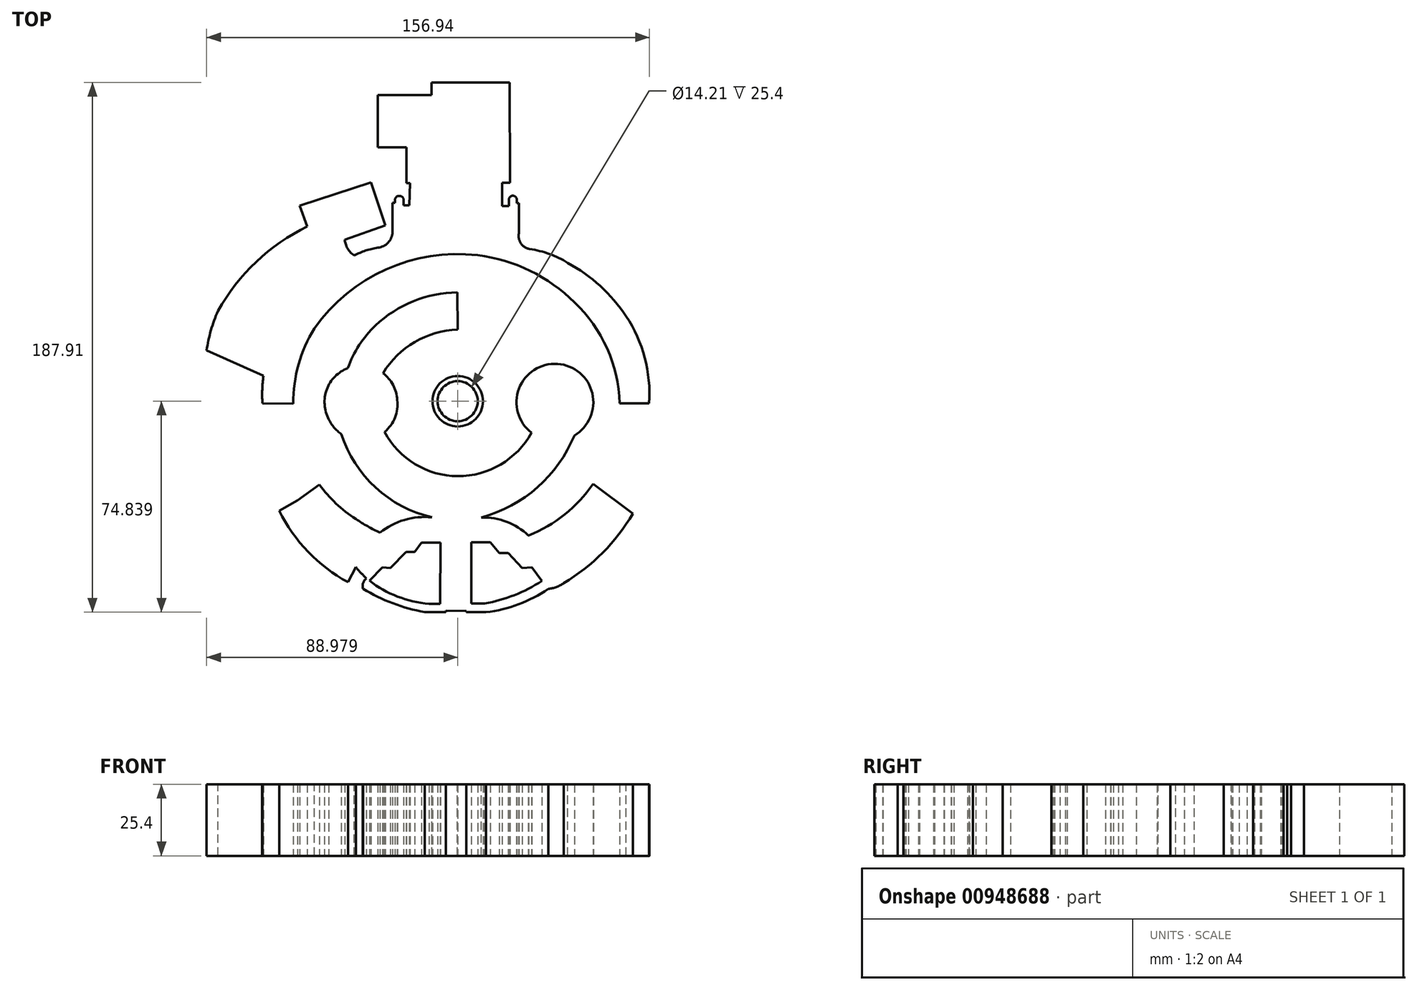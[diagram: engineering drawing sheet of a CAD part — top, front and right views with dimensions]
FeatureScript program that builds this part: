
annotation { "Feature Type Name" : "Feature", "Feature Type Description" : "" }
export const myFeature = defineFeature(function(context is Context, id is Id, definition is map)
    precondition{}
    {
        {
            var Q0;
            Q0=qCreatedBy(makeId("Top.planeOp"),FACE);
            var sketch = newSketch(context, id + "F0", { "sketchPlane" : qUnion([Q0])});
            skArc(sketch, "E0", {"start": v(181.34, -72.89) * mm, "mid": v(195.13, -62.13) * mm, "end": v(205.83, -48.3) * mm});
            skLineSegment(sketch, "E1", {"start": v(191.68, -37.7) * mm, "end": v(205.83, -48.3) * mm});
            skArc(sketch, "E2", {"start": v(163.15, -57.94) * mm, "mid": v(183.04, -47.44) * mm, "end": v(196.42, -29.36) * mm});
            skArc(sketch, "E3", {"start": v(185.16, 26.63) * mm, "mid": v(169.38, 37.88) * mm, "end": v(150.8, 43.4) * mm});
            skArc(sketch, "E4", {"start": v(150.8, 43.4) * mm, "mid": v(118.33, 38.35) * mm, "end": v(92.98, 17.42) * mm});
            skArc(sketch, "E5", {"start": v(92.98, 17.42) * mm, "mid": v(85.82, -2.9) * mm, "end": v(87.93, -24.34) * mm});
            skArc(sketch, "E6", {"start": v(87.91, -24.4) * mm, "mid": v(95.52, -39.01) * mm, "end": v(107.64, -50.16) * mm});
            skArc(sketch, "E7", {"start": v(107.64, -50.16) * mm, "mid": v(112.67, -53.24) * mm, "end": v(117.97, -55.82) * mm});
            skArc(sketch, "E8", {"start": v(181.34, -72.89) * mm, "mid": v(176.23, -63.57) * mm, "end": v(168.82, -55.95) * mm});
            skArc(sketch, "E9", {"start": v(168.82, -55.95) * mm, "mid": v(161.1, -51.17) * mm, "end": v(152.17, -49.6) * mm});
            skArc(sketch, "E10", {"start": v(134.6, -49.59) * mm, "mid": v(119, -53.1) * mm, "end": v(108.7, -65.31) * mm});
            skArc(sketch, "E11", {"start": v(86.91, -43.6) * mm, "mid": v(96.8, -55.47) * mm, "end": v(108.7, -65.31) * mm});
            skLineSegment(sketch, "E12", {"start": v(86.91, -43.6) * mm, "end": v(94.73, -37.96) * mm});
            skLineSegment(sketch, "E13", {"start": v(86.91, -43.6) * mm, "end": v(80.54, -47.31) * mm});
            skArc(sketch, "E14", {"start": v(153.32, -80.14) * mm, "mid": v(167.01, -75.81) * mm, "end": v(179.07, -68.01) * mm});
            skArc(sketch, "E15", {"start": v(174.88, -71.26) * mm, "mid": v(166, -60.08) * mm, "end": v(153.28, -53.59) * mm});
            skLineSegment(sketch, "E16", {"start": v(85.46, -9.22) * mm, "end": v(74.52, -9.11) * mm});
            skLineSegment(sketch, "E17", {"start": v(103.75, 48.85) * mm, "end": v(118.04, 53.91) * mm});
            skLineSegment(sketch, "E18", {"start": v(102.88, 40.88) * mm, "end": v(109.93, 33.78) * mm});
            skArc(sketch, "E19", {"start": v(102.88, 40.88) * mm, "mid": v(92.18, 32.67) * mm, "end": v(83.3, 22.5) * mm});
            skArc(sketch, "E20", {"start": v(115.4, 46.06) * mm, "mid": v(119.06, 47.83) * mm, "end": v(120.62, 51.59) * mm});
            skArc(sketch, "E21", {"start": v(107.09, 43.28) * mm, "mid": v(104.97, 42.1) * mm, "end": v(102.88, 40.88) * mm});
            skArc(sketch, "E22", {"start": v(115.4, 46.06) * mm, "mid": v(111.12, 45.04) * mm, "end": v(107.09, 43.28) * mm});
            skLineSegment(sketch, "E23", {"start": v(120.62, 51.59) * mm, "end": v(120.68, 62.02) * mm});
            skLineSegment(sketch, "E24", {"start": v(124.62, 61.04) * mm, "end": v(126.55, 61.04) * mm});
            skLineSegment(sketch, "E25", {"start": v(124.62, 61.04) * mm, "end": v(124.62, 62.9) * mm});
            skArc(sketch, "E26", {"start": v(124.62, 62.9) * mm, "mid": v(123.06, 64.44) * mm, "end": v(121.46, 62.94) * mm});
            skLineSegment(sketch, "E27", {"start": v(121.46, 62.94) * mm, "end": v(121.46, 62.02) * mm});
            skLineSegment(sketch, "E28", {"start": v(121.46, 62.02) * mm, "end": v(120.68, 62.02) * mm});
            skLineSegment(sketch, "E29", {"start": v(126.55, 61.04) * mm, "end": v(126.83, 68.99) * mm});
            skLineSegment(sketch, "E30", {"start": v(126.83, 68.99) * mm, "end": v(125.64, 68.99) * mm});
            skLineSegment(sketch, "E31", {"start": v(125.64, 68.99) * mm, "end": v(125.64, 81.66) * mm});
            skLineSegment(sketch, "E32", {"start": v(125.64, 81.66) * mm, "end": v(115.45, 81.66) * mm});
            skLineSegment(sketch, "E33", {"start": v(115.45, 81.66) * mm, "end": v(115.45, 100.23) * mm});
            skLineSegment(sketch, "E34", {"start": v(115.45, 100.23) * mm, "end": v(134.52, 100.15) * mm});
            skLineSegment(sketch, "E35", {"start": v(134.52, 100.15) * mm, "end": v(134.52, 104.68) * mm});
            skLineSegment(sketch, "E36", {"start": v(134.52, 104.68) * mm, "end": v(162.15, 104.68) * mm});
            skLineSegment(sketch, "E37", {"start": v(162.15, 104.68) * mm, "end": v(162.23, 69.1) * mm});
            skLineSegment(sketch, "E38", {"start": v(162.23, 69.1) * mm, "end": v(126.83, 68.99) * mm});
            skLineSegment(sketch, "E39", {"start": v(113.02, 69.24) * mm, "end": v(118.04, 53.91) * mm});
            skLineSegment(sketch, "E40", {"start": v(103.75, 48.85) * mm, "end": v(99.86, 57.36) * mm});
            skArc(sketch, "E41", {"start": v(103.75, 48.85) * mm, "mid": v(104.76, 45.67) * mm, "end": v(107.09, 43.28) * mm});
            skArc(sketch, "E42", {"start": v(83.3, 22.5) * mm, "mid": v(76.3, 7.42) * mm, "end": v(74.52, -9.11) * mm});
            skLineSegment(sketch, "E43", {"start": v(211.58, -9.1) * mm, "end": v(201.18, -9.1) * mm});
            skArc(sketch, "E44", {"start": v(211.58, -9.1) * mm, "mid": v(210.05, 6.99) * mm, "end": v(203.46, 21.74) * mm});
            skArc(sketch, "E45", {"start": v(201.18, -9.1) * mm, "mid": v(196.68, 10.37) * mm, "end": v(185.12, 26.66) * mm});
            skArc(sketch, "E46", {"start": v(203.46, 21.74) * mm, "mid": v(194.24, 32.44) * mm, "end": v(182.78, 40.69) * mm});
            skLineSegment(sketch, "E47", {"start": v(182.78, 40.69) * mm, "end": v(176.47, 33.78) * mm});
            skArc(sketch, "E48", {"start": v(182.78, 40.69) * mm, "mid": v(176.29, 43.82) * mm, "end": v(169.3, 45.58) * mm});
            skArc(sketch, "E49", {"start": v(165.42, 51.02) * mm, "mid": v(166.2, 47.48) * mm, "end": v(169.3, 45.58) * mm});
            skLineSegment(sketch, "E50", {"start": v(165.42, 51.02) * mm, "end": v(165.42, 61.82) * mm});
            skLineSegment(sketch, "E51", {"start": v(165.42, 61.82) * mm, "end": v(164.7, 61.82) * mm});
            skArc(sketch, "E52", {"start": v(164.7, 63.06) * mm, "mid": v(163.32, 64.5) * mm, "end": v(161.9, 63.1) * mm});
            skLineSegment(sketch, "E53", {"start": v(164.7, 61.82) * mm, "end": v(164.7, 63.06) * mm});
            skLineSegment(sketch, "E54", {"start": v(161.86, 61.64) * mm, "end": v(161.9, 63.1) * mm});
            skLineSegment(sketch, "E55", {"start": v(161.86, 61.64) * mm, "end": v(161.86, 60.79) * mm});
            skLineSegment(sketch, "E56", {"start": v(159.5, 60.81) * mm, "end": v(161.86, 60.79) * mm});
            skLineSegment(sketch, "E57", {"start": v(159.5, 60.81) * mm, "end": v(159.5, 69.1) * mm});
            skArc(sketch, "E58", {"start": v(80.54, -47.31) * mm, "mid": v(90.74, -61.82) * mm, "end": v(104.84, -72.58) * mm});
            skArc(sketch, "E59", {"start": v(110.18, -74.9) * mm, "mid": v(120.72, -80.08) * mm, "end": v(132.05, -83.17) * mm});
            skArc(sketch, "E60", {"start": v(196.42, -29.36) * mm, "mid": v(199.77, -19.46) * mm, "end": v(201.18, -9.1) * mm});
            skArc(sketch, "E61", {"start": v(99.86, 57.36) * mm, "mid": v(76.13, 44.37) * mm, "end": v(58.8, 23.61) * mm});
            skArc(sketch, "E62", {"start": v(100.87, 55.28) * mm, "mid": v(72.42, 38.03) * mm, "end": v(56.1, 9.03) * mm});
            skLineSegment(sketch, "E63", {"start": v(54.75, 9.64) * mm, "end": v(74.9, 0.57) * mm});
            skArc(sketch, "E64", {"start": v(54.75, 9.64) * mm, "mid": v(56.28, 16.77) * mm, "end": v(58.8, 23.61) * mm});
            skArc(sketch, "E65", {"start": v(177.16, -64.9) * mm, "mid": v(189.55, -55.53) * mm, "end": v(198.76, -43) * mm});
            skLineSegment(sketch, "E66", {"start": v(146.81, -54.77) * mm, "end": v(146.79, -83.13) * mm});
            skLineSegment(sketch, "E67", {"start": v(146.76, -83.13) * mm, "end": v(153.82, -83.23) * mm});
            skLineSegment(sketch, "E68", {"start": v(153.32, -80.14) * mm, "end": v(148.5, -80.15) * mm});
            skLineSegment(sketch, "E69", {"start": v(148.5, -80.15) * mm, "end": v(148.5, -58.44) * mm});
            skLineSegment(sketch, "E70", {"start": v(148.5, -58.44) * mm, "end": v(155.27, -58.44) * mm});
            skLineSegment(sketch, "E71", {"start": v(155.27, -58.44) * mm, "end": v(158.48, -62.21) * mm});
            skLineSegment(sketch, "E72", {"start": v(158.48, -62.21) * mm, "end": v(161.64, -62.21) * mm});
            skLineSegment(sketch, "E73", {"start": v(161.64, -62.21) * mm, "end": v(166.6, -67.58) * mm});
            skLineSegment(sketch, "E74", {"start": v(166.6, -67.58) * mm, "end": v(170, -67.3) * mm});
            skLineSegment(sketch, "E75", {"start": v(170, -67.3) * mm, "end": v(173.55, -72.16) * mm});
            skLineSegment(sketch, "E76", {"start": v(132.05, -83.17) * mm, "end": v(139.5, -83.17) * mm});
            skLineSegment(sketch, "E77", {"start": v(139.5, -54.78) * mm, "end": v(139.5, -83.17) * mm});
            skLineSegment(sketch, "E78", {"start": v(135.83, -54.78) * mm, "end": v(139.5, -54.78) * mm});
            skLineSegment(sketch, "E79", {"start": v(135.83, -54.78) * mm, "end": v(133.7, -53.48) * mm});
            skArc(sketch, "E80", {"start": v(133.7, -53.48) * mm, "mid": v(120.38, -59.61) * mm, "end": v(111.4, -71.2) * mm});
            skLineSegment(sketch, "E81", {"start": v(122.9, -57.82) * mm, "end": v(117.97, -55.82) * mm});
            skLineSegment(sketch, "E82", {"start": v(137.62, -58.54) * mm, "end": v(137.58, -80.27) * mm});
            skLineSegment(sketch, "E83", {"start": v(137.58, -80.27) * mm, "end": v(133.57, -80.27) * mm});
            skArc(sketch, "E84", {"start": v(112.45, -72.07) * mm, "mid": v(122.43, -77.67) * mm, "end": v(133.57, -80.27) * mm});
            skLineSegment(sketch, "E85", {"start": v(137.62, -58.54) * mm, "end": v(130.97, -58.6) * mm});
            skLineSegment(sketch, "E86", {"start": v(128.48, -61.87) * mm, "end": v(130.97, -58.6) * mm});
            skLineSegment(sketch, "E87", {"start": v(128.48, -61.87) * mm, "end": v(125.43, -61.85) * mm});
            skLineSegment(sketch, "E88", {"start": v(125.43, -61.85) * mm, "end": v(119.85, -67.57) * mm});
            skLineSegment(sketch, "E89", {"start": v(119.85, -67.57) * mm, "end": v(117.02, -67.37) * mm});
            skLineSegment(sketch, "E90", {"start": v(112.45, -72.07) * mm, "end": v(117.02, -67.37) * mm});
            skArc(sketch, "E91", {"start": v(107.68, -67.25) * mm, "mid": v(109.92, -69.8) * mm, "end": v(112.45, -72.07) * mm});
            skArc(sketch, "E92", {"start": v(111.4, -71.2) * mm, "mid": v(110.21, -72.86) * mm, "end": v(110.18, -74.9) * mm});
            skLineSegment(sketch, "E93", {"start": v(139.5, -82.7) * mm, "end": v(146.79, -82.85) * mm});
            skLineSegment(sketch, "E94", {"start": v(139.5, -56.49) * mm, "end": v(146.81, -56.5) * mm});
            skLineSegment(sketch, "E95", {"start": v(113.02, 69.24) * mm, "end": v(87.73, 60.93) * mm});
            skLineSegment(sketch, "E96", {"start": v(87.73, 60.93) * mm, "end": v(90.43, 53.55) * mm});
            skArc(sketch, "E97", {"start": v(156.54, 66.9) * mm, "mid": v(143.55, 68.06) * mm, "end": v(130.54, 66.99) * mm});
            skArc(sketch, "E98", {"start": v(130.54, 66.99) * mm, "mid": v(128.75, 67.4) * mm, "end": v(127.8, 68.99) * mm});
            skArc(sketch, "E99", {"start": v(156.54, 66.9) * mm, "mid": v(158.14, 67.46) * mm, "end": v(158.61, 69.1) * mm});
            skLineSegment(sketch, "E100", {"start": v(146.81, -54.77) * mm, "end": v(150.5, -54.77) * mm});
            skLineSegment(sketch, "E101", {"start": v(150.5, -54.77) * mm, "end": v(153.28, -53.59) * mm});
            skArc(sketch, "E102", {"start": v(153.82, -83.23) * mm, "mid": v(165.34, -80.44) * mm, "end": v(175.85, -74.95) * mm});
            skArc(sketch, "E103", {"start": v(175.85, -74.95) * mm, "mid": v(176.08, -72.91) * mm, "end": v(174.88, -71.26) * mm});
            skArc(sketch, "E104", {"start": v(110.18, -74.9) * mm, "mid": v(107.33, -74.15) * mm, "end": v(104.84, -72.58) * mm});
            skArc(sketch, "E105", {"start": v(175.85, -74.95) * mm, "mid": v(178.74, -74.3) * mm, "end": v(181.34, -72.89) * mm});
            skArc(sketch, "E106", {"start": v(152.17, -49.6) * mm, "mid": v(172.03, -38.9) * mm, "end": v(185.08, -20.52) * mm});
            skArc(sketch, "E107", {"start": v(184.66, 3.24) * mm, "mid": v(168.88, 24.5) * mm, "end": v(143.68, 32.59) * mm});
            skCircle(sketch, "E108", {"center": v(178.21, -8.76) * mm, "radius": 13.62 * mm});
            skArc(sketch, "E109", {"start": v(122.31, -7.95) * mm, "mid": v(105.92, 3.71) * mm, "end": v(98.08, -14.82) * mm});
            skArc(sketch, "E110", {"start": v(98.08, -14.82) * mm, "mid": v(113.14, -21.78) * mm, "end": v(122.31, -7.95) * mm});
            skArc(sketch, "E111", {"start": v(143.68, 32.59) * mm, "mid": v(118.18, 24.08) * mm, "end": v(102.56, 2.21) * mm});
            skArc(sketch, "E112", {"start": v(102.52, -20.07) * mm, "mid": v(114.67, -39.05) * mm, "end": v(134.6, -49.59) * mm});
            skArc(sketch, "E113", {"start": v(169.52, 1.72) * mm, "mid": v(158.78, 13.01) * mm, "end": v(143.72, 16.99) * mm});
            skArc(sketch, "E114", {"start": v(143.72, 16.99) * mm, "mid": v(128.54, 12.62) * mm, "end": v(117.26, 1.56) * mm});
            skArc(sketch, "E115", {"start": v(117.82, -19.3) * mm, "mid": v(143.78, -34.98) * mm, "end": v(169.88, -19.54) * mm});
            skCircle(sketch, "E116", {"center": v(143.76, -8.41) * mm, "radius": 8.94 * mm});
            skCircle(sketch, "E117", {"center": v(143.73, -8.4) * mm, "radius": 7.1 * mm});
            skArc(sketch, "E118", {"start": v(114.61, 18.48) * mm, "mid": v(108.81, 11.49) * mm, "end": v(104.8, 3.34) * mm});
            skArc(sketch, "E119", {"start": v(143.65, 30.2) * mm, "mid": v(128.03, 27.07) * mm, "end": v(114.61, 18.48) * mm});
            skArc(sketch, "E120", {"start": v(173.16, 18.34) * mm, "mid": v(159.52, 27.04) * mm, "end": v(143.65, 30.2) * mm});
            skArc(sketch, "E121", {"start": v(182.25, 4.25) * mm, "mid": v(178.42, 11.76) * mm, "end": v(173.16, 18.34) * mm});
            skLineSegment(sketch, "E122", {"start": v(173.02, -36.4) * mm, "end": v(163.92, -27.18) * mm});
            skLineSegment(sketch, "E123", {"start": v(163.87, 9.16) * mm, "end": v(172.93, 18.55) * mm});
            skLineSegment(sketch, "E124", {"start": v(143.72, 16.99) * mm, "end": v(143.65, 30.2) * mm});
            skLineSegment(sketch, "E125", {"start": v(114.92, 18.76) * mm, "end": v(123.73, 9.18) * mm});
            skLineSegment(sketch, "E126", {"start": v(134.6, -49.59) * mm, "end": v(152.17, -49.6) * mm});
            skLineSegment(sketch, "E127", {"start": v(114.18, -36.64) * mm, "end": v(123.88, -27.15) * mm});
            skArc(sketch, "E128", {"start": v(105.05, -21.4) * mm, "mid": v(108.62, -29.6) * mm, "end": v(114.18, -36.64) * mm});
            skArc(sketch, "E129", {"start": v(114.18, -36.64) * mm, "mid": v(143.64, -47.8) * mm, "end": v(173.02, -36.4) * mm});
            skArc(sketch, "E130", {"start": v(173.02, -36.4) * mm, "mid": v(178.55, -29.69) * mm, "end": v(182.18, -21.79) * mm});
            skLineSegment(sketch, "E131", {"start": v(143.92, -34.98) * mm, "end": v(143.85, -47.8) * mm});
            skLineSegment(sketch, "E132", {"start": v(104.84, -72.58) * mm, "end": v(108.7, -65.31) * mm});
            skSolve(sketch);
        }
        {
            var Q0;
            Q0 = qSketchRegion(id + "F0", true);
            extrude(context, id + "F1", {"entities" : qUnion([Q0]), "depth" : 25.4 * mm, "offsetDistance" : 25.4 * mm});
        }
    });
